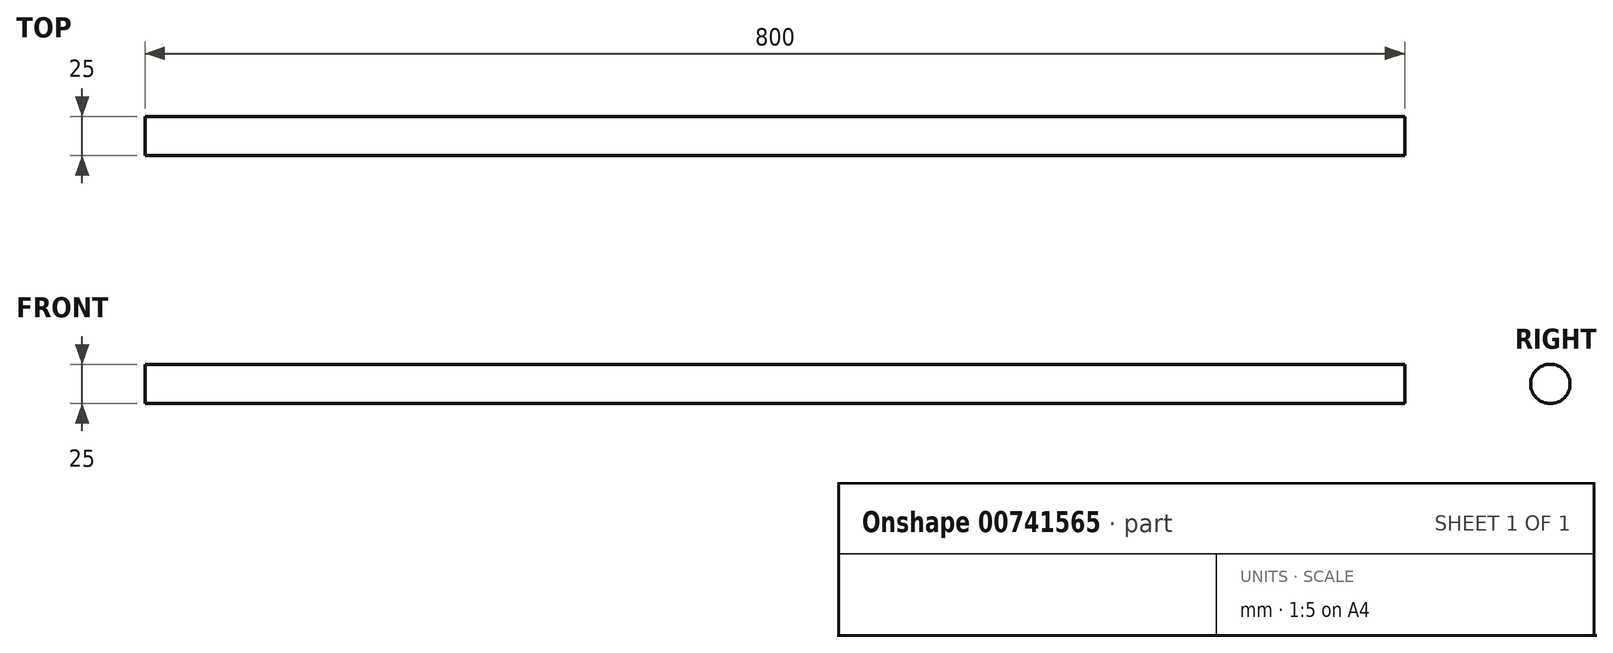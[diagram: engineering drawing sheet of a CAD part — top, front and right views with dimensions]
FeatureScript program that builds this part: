
annotation { "Feature Type Name" : "Feature", "Feature Type Description" : "" }
export const myFeature = defineFeature(function(context is Context, id is Id, definition is map)
    precondition{}
    {
        {
            var Q0;
            Q0=qCreatedBy(makeId("Right.planeOp"),FACE);
            var sketch = newSketch(context, id + "F0", { "sketchPlane" : qUnion([Q0])});
            skCircle(sketch, "E0", {"center": v(0, 0) * mm, "radius": 12.5 * mm});
            skSolve(sketch);
        }
        {
            var Q0;
            Q0=qSketchRegion(id+"F0",true);
            extrude(context, id + "F1", {"entities" : qUnion([Q0]), "depth" : 800 * mm, "offsetDistance" : 25 * mm});
        }
    });
